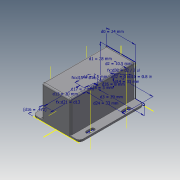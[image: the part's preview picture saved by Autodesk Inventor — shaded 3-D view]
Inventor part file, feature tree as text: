
AUTODESK INVENTOR PART (.ipt)
format: ipt  version: 2020.3 (Build 243373000, 373)  size: 205,312 bytes
history: native  units: in
note: dims shown in document units (in); Inventor stores cm internally (conversion verified against a paired STEP export)
features: other x5, extrude x3, fillet x3, sketch x2
ambient origin geometry x8: Origin, YZ Plane, XZ Plane, XY Plane, X Axis, Y Axis, Z Axis, Center Point
bodies: Solid1 (feature_tree)
feature tree (13):
  sketch  "Sketch1"  dims[d0=0.9449in d1=1.1024in]
  extrude  "Extrusion1"  Depth=1.1024in
  extrude  "Extrusion3"  Depth=0.05in
  sketch  "Sketch3"  dims[d2=0.4134in d3=1.5354in d4=0.0591in d5=2.126in d6=0.0in d10=0.8in d11=0.0394in d12=0.0in d13=1.1811in d14=1.2992in d15=0.4724in d16=0.4724in d17=0.2756in d18=0.1181in d19=0.7874in d21=1.1811in d22=0.7874in d24=1.2992in d27=0.0394in d28=0.0in d29=0.125in d30=0.2067in d32=0.0in d35=0.315in d36=0.05in d37=0.05in]
  extrude  "Extrusion4"  Depth=0.05in
  fillet  "Fillet1"  Radius=2.126in
  other  "Work Axis1"
  other  "Work Axis2"
  other  "Work Axis3"
  other  "Work Axis4"
  other  "Work Axis5"
  fillet  "Fillet2"  Radius=0.8in
  fillet  "Fillet3"  Radius=0.0394in
